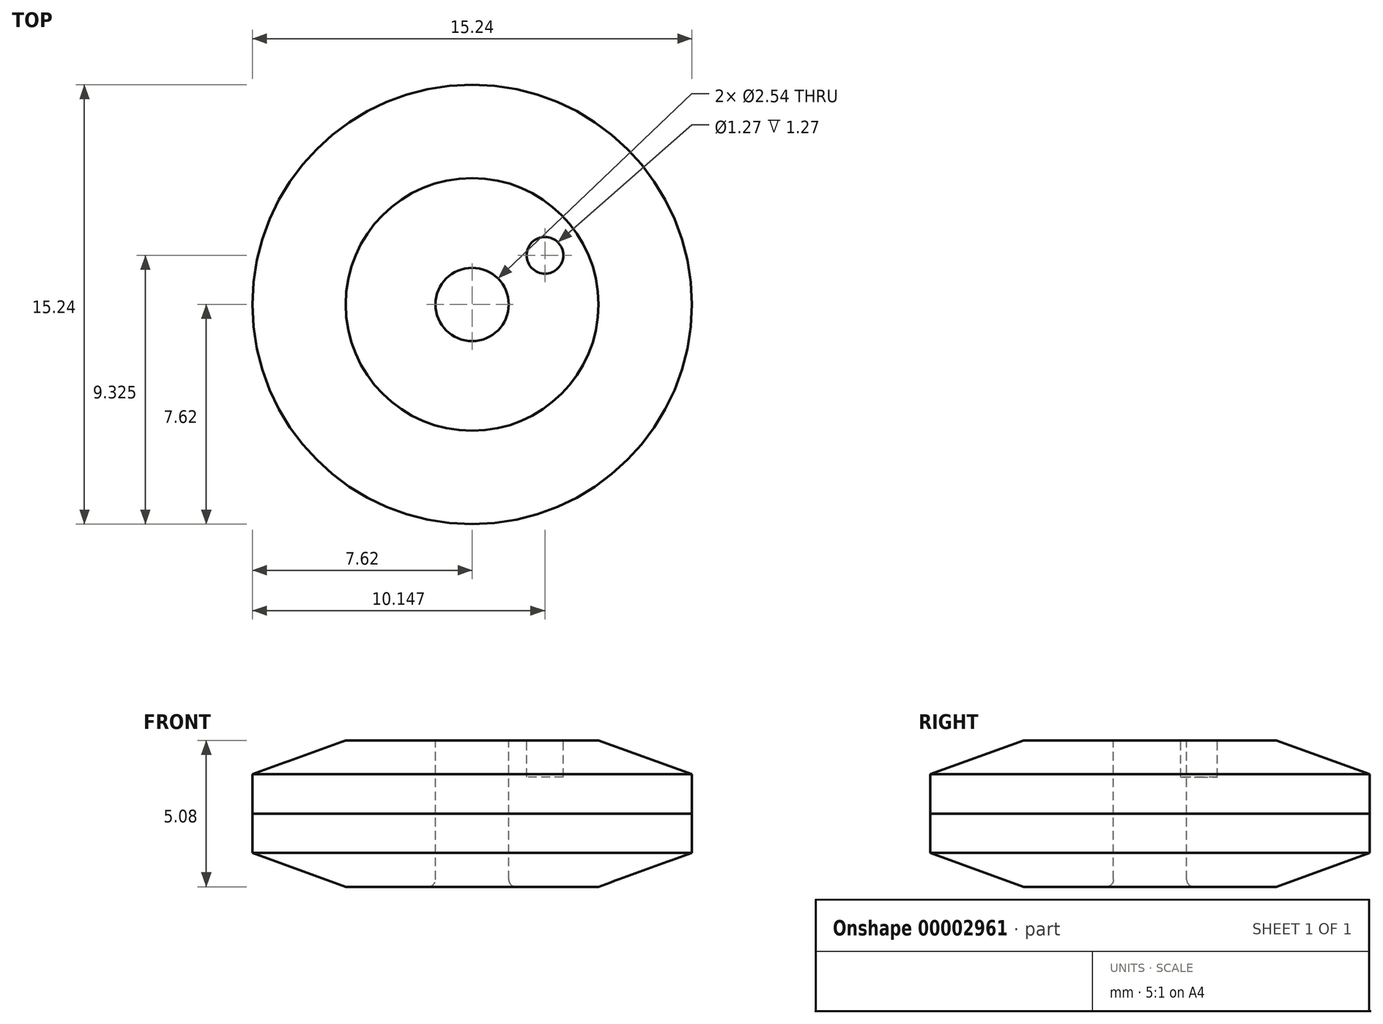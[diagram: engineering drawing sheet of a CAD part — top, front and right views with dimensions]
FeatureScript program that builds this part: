
annotation { "Feature Type Name" : "Feature", "Feature Type Description" : "" }
export const myFeature = defineFeature(function(context is Context, id is Id, definition is map)
    precondition{}
    {
        {
            var Q0;
            Q0=qCreatedBy(makeId("Top.planeOp"),FACE);
            var sketch = newSketch(context, id + "F0", { "sketchPlane" : qUnion([Q0])});
            skCircle(sketch, "E0", {"center": v(0, 0) * mm, "radius": 7.62 * mm});
            skSolve(sketch);
        }
        {
            var Q0;
            Q0=makeQuery(id+"F0.imprint","IMPRINT",FACE,{"disambiguationData":[TD([[makeQuery(id+"F0.imprint","IMPRINT",EDGE,{"derivedFrom":sQuery(id+"F0.wireOp",EDGE,"E0")}),1.0]])]});
            extrude(context, id + "F1", {"entities" : qUnion([Q0]), "depth" : 2.54 * mm});
        }
        {
            var Q0;
            Q0=makeQuery(id+"F1.opExtrude","SWEPT_BODY",BODY,{"disambiguationData":[OSD([sQuery(id+"F0.wireOp",EDGE,"E0")])]});
            var Q1;
            Q1=qCreatedBy(makeId("Top.planeOp"),FACE);
            mirror(context, id + "F2", {"entities" : qUnion([Q0]), "mirrorPlane" : qUnion([Q1])});
        }
        {
            var Q0;
            Q0=makeQuery(id+"F1.opExtrude","CAP_FACE",FACE,{"disambiguationData":[OSD([sQuery(id+"F0.wireOp",EDGE,"E0")])],"isStart":false});
            var sketch = newSketch(context, id + "F3", { "sketchPlane" : qUnion([Q0])});
            skCircle(sketch, "E1", {"center": v(0, 0) * mm, "radius": 1.27 * mm});
            skSolve(sketch);
        }
        {
            var Q0;
            Q0=makeQuery(id+"F3.imprint","IMPRINT",FACE,{"disambiguationData":[TD([[makeQuery(id+"F3.imprint","IMPRINT",EDGE,{"derivedFrom":sQuery(id+"F3.wireOp",EDGE,"E1")}),1.0]])]});
            extrude(context, id + "F4", {"entities" : qUnion([Q0]), "operationType" : NewBodyOperationType.REMOVE, "endBound" : BoundingType.THROUGH_ALL, "oppositeDirection" : true, "depth" : 25.4 * mm});
        }
        {
            var Q0;
            Q0=makeQuery(id+"F4.boolean.opBoolean","COPY",EDGE,{"derivedFrom":makeQuery(id+"F4.opExtrude","CAP_EDGE",EDGE,{"disambiguationData":[OSD([sQuery(id+"F3.wireOp",EDGE,"E1")])],"isStart":true})});
            var Q1;
            Q1=makeQuery(id+"F1.opExtrude","CAP_EDGE",EDGE,{"disambiguationData":[OSD([sQuery(id+"F0.wireOp",EDGE,"E0")])],"isStart":false});
            var Q2;
            Q2=makeQuery(id+"F2.opPattern","COPY",EDGE,{"derivedFrom":makeQuery(id+"F1.opExtrude","CAP_EDGE",EDGE,{"disambiguationData":[OSD([sQuery(id+"F0.wireOp",EDGE,"E0")])],"isStart":false}),"instanceName":"1"});
            var Q3;
            Q3=makeQuery(id+"F4.boolean.opBoolean","INTERSECT",EDGE,{"derivedFrom":[makeQuery(id+"F2.opPattern","COPY",FACE,{"derivedFrom":makeQuery(id+"F1.opExtrude","CAP_FACE",FACE,{"disambiguationData":[OSD([sQuery(id+"F0.wireOp",EDGE,"E0")])],"isStart":false}),"instanceName":"1"}),makeQuery(id+"F4.opExtrude","SWEPT_FACE",FACE,{"disambiguationData":[OSD([sQuery(id+"F3.wireOp",EDGE,"E1")])]})]});
            fillet(context, id + "F5", {"entities" : qUnion([Q0, Q1, Q2, Q3]), "radius" : 0.25 * mm, "tangentPropagation" : true, "allowEdgeOverflow" : false});
        }
        {
            var Q0;
            Q0=makeQuery(id+"F3.imprint","IMPRINT",FACE,{"disambiguationData":[TD([[makeQuery(id+"F3.imprint","IMPRINT",EDGE,{"derivedFrom":sQuery(id+"F3.wireOp",EDGE,"E1")}),-1.0]])]});
            var sketch = newSketch(context, id + "F6", { "sketchPlane" : qUnion([Q0])});
            skCircle(sketch, "E2", {"center": v(2.53, 1.7) * mm, "radius": 0.64 * mm});
            skSolve(sketch);
        }
        {
            var Q0;
            Q0=makeQuery(id+"F6.imprint","IMPRINT",FACE,{"disambiguationData":[TD([[makeQuery(id+"F6.imprint","IMPRINT",EDGE,{"derivedFrom":sQuery(id+"F6.wireOp",EDGE,"E2")}),1.0]])]});
            extrude(context, id + "F7", {"entities" : qUnion([Q0]), "operationType" : NewBodyOperationType.REMOVE, "oppositeDirection" : true, "depth" : 1.27 * mm});
        }
        {
            var Q0;
            Q0=qCreatedBy(makeId("Front.planeOp"),FACE);
            var sketch = newSketch(context, id + "F8", { "sketchPlane" : qUnion([Q0])});
            skLineSegment(sketch, "E3", {"start": v(7.87, 0) * mm, "end": v(7.87, 2.54) * mm});
            skLineSegment(sketch, "E4", {"start": v(7.87, 2.54) * mm, "end": v(4.38, 2.54) * mm});
            skLineSegment(sketch, "E5.0.MirrorCS", {"start": v(7.87, 0) * mm, "end": v(7.87, -2.54) * mm});
            skLineSegment(sketch, "E6.0.MirrorCS", {"start": v(7.87, -2.54) * mm, "end": v(4.38, -2.54) * mm});
            skLineSegment(sketch, "E7", {"start": v(4.38, 2.54) * mm, "end": v(7.87, 1.27) * mm});
            skLineSegment(sketch, "E8", {"start": v(4.38, -2.54) * mm, "end": v(7.87, -1.27) * mm});
            skSolve(sketch);
        }
        {
            var Q0;
            {var subQ1=sQuery(id+"F8.wireOp",EDGE,"E4");Q0=makeQuery(id+"F8.imprint","IMPRINT",FACE,{"disambiguationData":[TD([[makeQuery(id+"F8.imprint","IMPRINT",EDGE,{"derivedFrom":subQ1}),1.0]])]});}
            var Q1;
            {var subQ1=sQuery(id+"F8.wireOp",EDGE,"E6.0.MirrorCS");Q1=makeQuery(id+"F8.imprint","IMPRINT",FACE,{"disambiguationData":[TD([[makeQuery(id+"F8.imprint","IMPRINT",EDGE,{"derivedFrom":subQ1}),-1.0]])]});}
            var Q2;
            Q2=sQuery(id+"F3.wireOp",EDGE,"E1");
            revolve(context, id + "F9", {"operationType" : NewBodyOperationType.REMOVE, "entities" : qUnion([Q0, Q1]), "axis" : qUnion([Q2]), "revolveType" : RevolveType.FULL, "oppositeDirection" : true});
        }
    });
